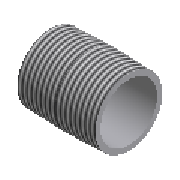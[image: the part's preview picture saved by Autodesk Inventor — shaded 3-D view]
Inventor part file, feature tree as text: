
AUTODESK INVENTOR PART (.ipt)
format: ipt  version: 2023.2 (Build 272271030, 271C)  size: 177,152 bytes
history: native  units: mm (DEFAULTED — no unit token found)
features: other x6, revolve x1, sketch x1
ambient origin geometry x8: Origin, YZ Plane, XZ Plane, XY Plane, X Axis, Y Axis, Z Axis, Center Point
bodies: Solid1 (feature_tree)
feature tree (8):
  revolve  "Revolution1"  Angle=90.0deg
  other  "Work Point1"
  other  "Work Axis1"
  other  "Work Point2"
  other  "Work Axis2"
  other  "Work Point3"
  other  "Work Point4"
  sketch  "Sketch1"  dims[d0=41.6mm d12=90.0deg d1=0.312398mm d2=44.0mm d3=0.0mm d4=0.0mm d5=0.0mm d6=0.0mm d7=12.7mm d8=47.803mm]
